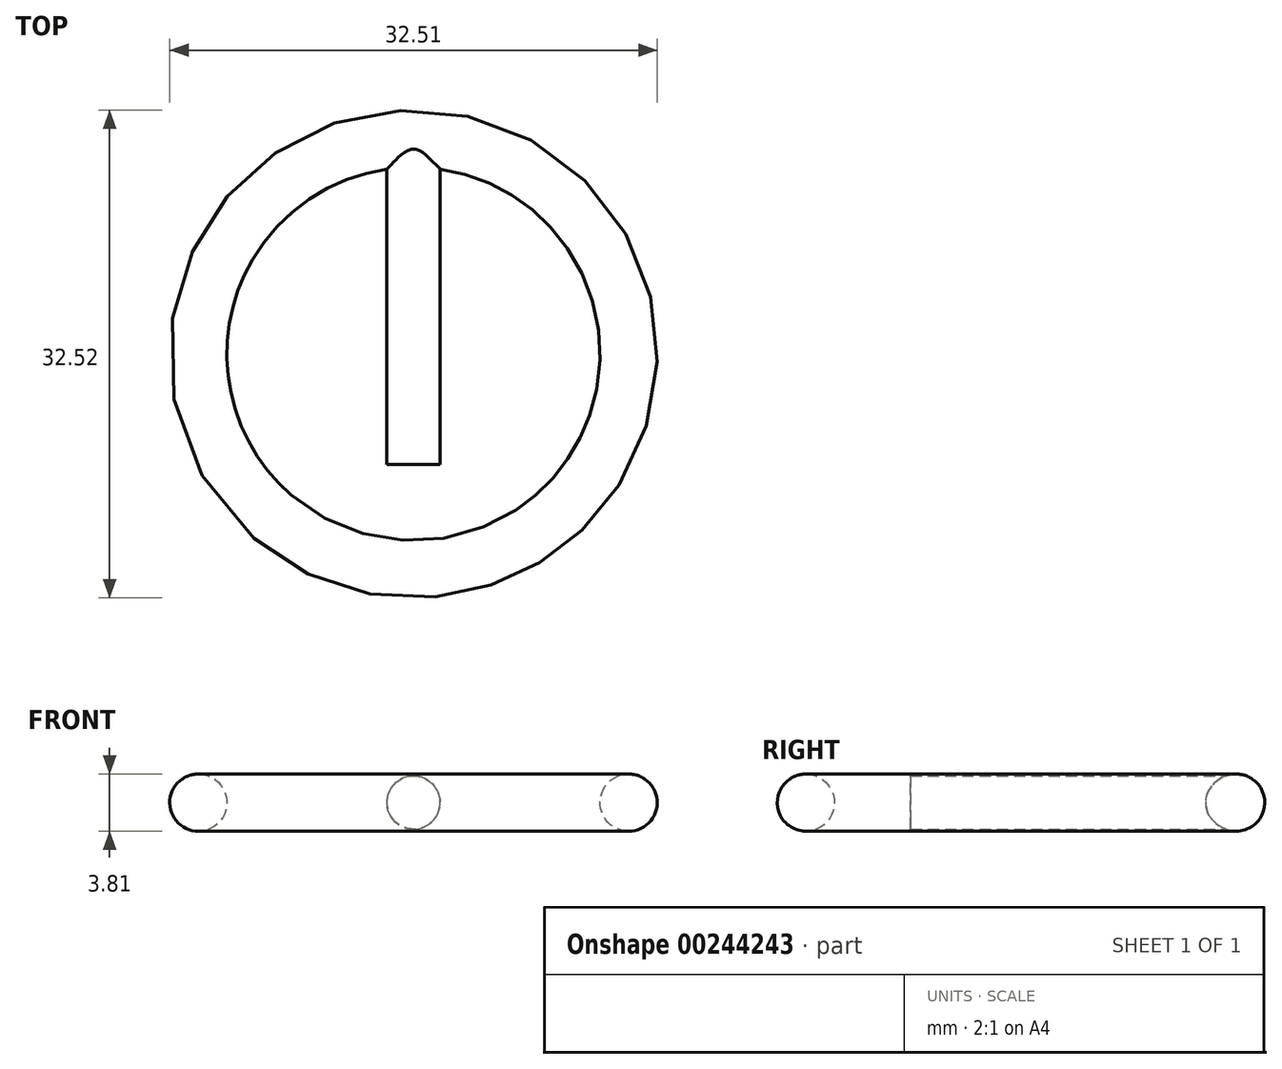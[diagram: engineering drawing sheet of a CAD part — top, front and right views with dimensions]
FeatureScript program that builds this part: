
annotation { "Feature Type Name" : "Feature", "Feature Type Description" : "" }
export const myFeature = defineFeature(function(context is Context, id is Id, definition is map)
    precondition{}
    {
        {
            var Q0;
            Q0=qCreatedBy(makeId("Front.planeOp"),FACE);
            var sketch = newSketch(context, id + "F0", { "sketchPlane" : qUnion([Q0])});
            skCircle(sketch, "E0", {"center": v(-41.36, 37.06) * mm, "radius": 1.78 * mm});
            skSolve(sketch);
        }
        {
            var Q0;
            Q0 = qSketchRegion(id + "F0", true);
            extrude(context, id + "F1", {"entities" : qUnion([Q0]), "depth" : 7.37 * mm});
        }
        {
            var Q0;
            Q0=makeQuery(id+"F1.opExtrude","CAP_FACE",FACE,{"disambiguationData":[OSD([sQuery(id+"F0.wireOp",EDGE,"E0")])],"isStart":false});
            var sketch = newSketch(context, id + "F2", { "sketchPlane" : qUnion([Q0])});
            skPoint(sketch, "E1", {"position": v(-41.36, 37.06) * mm});
            skSolve(sketch);
        }
        {
            var Q0;
            Q0=qCreatedBy(makeId("Front.planeOp"),FACE);
            var sketch = newSketch(context, id + "F3", { "sketchPlane" : qUnion([Q0])});
            skCircle(sketch, "E2", {"center": v(-27.01, 37.06) * mm, "radius": 1.9 * mm});
            skSolve(sketch);
        }
        {
            var Q0;
            Q0=makeQuery(id+"F1.opExtrude","CAP_FACE",FACE,{"disambiguationData":[OSD([sQuery(id+"F0.wireOp",EDGE,"E0")])],"isStart":true});
            var sketch = newSketch(context, id + "F4", { "sketchPlane" : qUnion([Q0])});
            skLineSegment(sketch, "E3", {"start": v(41.36, 37.06) * mm, "end": v(41.36, 38.84) * mm});
            skLineSegment(sketch, "E4", {"start": v(41.36, 37.06) * mm, "end": v(41.36, 35.28) * mm});
            skSolve(sketch);
        }
        {
            var Q0;
            Q0=makeQuery(id+"F3.imprint","IMPRINT",FACE,{"disambiguationData":[TD([[makeQuery(id+"F3.imprint","IMPRINT",EDGE,{"derivedFrom":sQuery(id+"F3.wireOp",EDGE,"E2")}),1.0]])]});
            var Q1;
            Q1=sQuery(id+"F4.wireOp",EDGE,"E4");
            revolve(context, id + "F5", {"entities" : qUnion([Q0]), "axis" : qUnion([Q1]), "revolveType" : RevolveType.FULL});
        }
        {
            var Q0;
            Q0=makeQuery(id+"F1.opExtrude","CAP_FACE",FACE,{"disambiguationData":[OSD([sQuery(id+"F0.wireOp",EDGE,"E0")])],"isStart":true});
            extrude(context, id + "F6", {"entities" : qUnion([Q0]), "operationType" : NewBodyOperationType.ADD, "depth" : 13.97 * mm});
        }
    });
